# Revit family: 903-20-001 DN65-600
name_source: partatom
category: Pipe Accessories
units: mm (PartAtom-declared; Revit-internal decimal feet)

## family parameters
Always vertical = Yes
Cut with Voids When Loaded = No
Part Type = Valve - Breaks Into
Round Connector Dimension = Use Diameter
Shared = No
Work Plane-Based = No

## types (21) — shared parameters
1 = 1 mm  [stored 0.00328084 ft]
DN065_PN10/16 = 903-065-20-11000
DN080_PN10/16 = 903-080-20-11000
DN100_PN10/16 = 903-100-20-11000
DN125_PN10/16 = 903-125-20-11000
DN150_PN10/16 = 903-150-20-11000
DN200_PN10 = 903-200-20-01000
DN200_PN16 = 903-200-20-11000
DN250_PN10 = 903-250-20-01000
DN250_PN16 = 903-250-20-11000
DN300_PN10 = 903-300-20-01000
DN300_PN16 = 903-300-20-11000
DN350_PN10 = 903-350-20-01000
DN350_PN16 = 903-350-20-11000
DN400_PN10 = 903-400-20-01000
DN400_PN16 = 903-400-20-11000
DN450_PN10 = 903-450-20-01000
DN450_PN16 = 903-450-20-11000
DN500_PN10 = 903-500-20-01000
DN500_PN16 = 903-500-20-11000
DN600_PN10 = 903-600-20-01000
DN600_PN16 = 903-600-20-11000
Description_ = AVK SILENT CHECK VALVE, PN10/16
Search_table = 903-20-001 DN65-600
URL product pages = https://www.avkvalves.com
zero-valued in all types: Default Elevation

## per-type parameters (varying)
| type | Bodywall_thickness | C | C1 | D2 | DN | FL_T | Flange_thickness | Flange_thickness_2 | Flange_thickness_3 | ID | ID-1 | L | L/2 | L3 | L_ref | L_ref_2 | W | W1 | W2 | dim1 | dim2 | dim3 | w4 | wall_T |
| DN065_PN10/16 | 43 mm | 28 mm  [stored 0.0918635 ft] | 25 mm  [stored 0.082021 ft] | 69 mm | 65 mm | 4 mm  [stored 0.0131234 ft] | 19 mm  [stored 0.062336 ft] | 10 mm  [stored 0.0328084 ft] | 29 mm | 33 mm  [stored 0.108268 ft] | 32 mm | 140 mm | 70 mm | 42 mm  [stored 0.137795 ft] | 20 mm  [stored 0.0656168 ft] | 15 mm  [stored 0.0492126 ft] | 93 mm | 46 mm | 52 mm | 27 mm  [stored 0.0885827 ft] | 16 mm  [stored 0.0524934 ft] | 13 mm  [stored 0.0426509 ft] | 83 mm | 10 mm  [stored 0.0328084 ft] |
| DN080_PN10/16 | 50 mm | 36 mm | 32 mm | 75 mm | 80 mm | 4 mm  [stored 0.0131234 ft] | 19 mm  [stored 0.062336 ft] | 10 mm  [stored 0.0328084 ft] | 29 mm | 40 mm  [stored 0.131234 ft] | 39 mm  [stored 0.127953 ft] | 152 mm | 76 mm | 46 mm | 15 mm  [stored 0.0492126 ft] | 20 mm  [stored 0.0656168 ft] | 100 mm | 49 mm | 57 mm | 27 mm  [stored 0.0885827 ft] | 16 mm  [stored 0.0524934 ft] | 13 mm  [stored 0.0426509 ft] | 90 mm | 10 mm  [stored 0.0328084 ft] |
| DN100_PN10/16 | 60 mm | 46 mm | 41 mm | 88 mm | 100 mm | 4 mm  [stored 0.0131234 ft] | 19 mm  [stored 0.062336 ft] | 10 mm  [stored 0.0328084 ft] | 29 mm | 50 mm | 49 mm | 184 mm | 92 mm | 55 mm | 20 mm  [stored 0.0656168 ft] | 20 mm  [stored 0.0656168 ft] | 118 mm | 60 mm | 69 mm | 30 mm  [stored 0.0984252 ft] | 18 mm | 15 mm  [stored 0.0492126 ft] | 106 mm | 10 mm  [stored 0.0328084 ft] |
| DN125_PN10/16 | 73 mm | 51 mm | 46 mm | 101 mm | 125 mm | 4 mm  [stored 0.0131234 ft] | 19 mm  [stored 0.062336 ft] | 10 mm  [stored 0.0328084 ft] | 29 mm | 63 mm | 62 mm | 216 mm | 108 mm | 65 mm | 20 mm  [stored 0.0656168 ft] | 25 mm  [stored 0.082021 ft] | 135 mm | 70 mm | 81 mm | 33 mm  [stored 0.108268 ft] | 20 mm  [stored 0.0656168 ft] | 16 mm  [stored 0.0524934 ft] | 122 mm | 10 mm  [stored 0.0328084 ft] |
| DN150_PN10/16 | 85 mm | 61 mm | 55 mm | 113 mm | 150 mm | 4 mm  [stored 0.0131234 ft] | 19 mm  [stored 0.062336 ft] | 10 mm  [stored 0.0328084 ft] | 29 mm | 75 mm | 74 mm | 248 mm | 124 mm | 74 mm | 25 mm  [stored 0.082021 ft] | 35 mm  [stored 0.114829 ft] | 150 mm | 81 mm | 93 mm | 34 mm | 20 mm  [stored 0.0656168 ft] | 16 mm  [stored 0.0524934 ft] | 135 mm | 10 mm  [stored 0.0328084 ft] |
| DN200_PN10 | 110 mm | 84 mm | 76 mm | 135 mm | 200 mm | 4 mm  [stored 0.0131234 ft] | 20 mm  [stored 0.0656168 ft] | 10 mm  [stored 0.0328084 ft] | 30 mm  [stored 0.0984252 ft] | 100 mm | 99 mm | 317 mm | 159 mm | 95 mm | 40 mm  [stored 0.131234 ft] | 30 mm  [stored 0.0984252 ft] | 180 mm | 103 mm | 118 mm | 36 mm | 22 mm  [stored 0.0721785 ft] | 17 mm | 162 mm | 10 mm  [stored 0.0328084 ft] |
| DN200_PN16 | 110 mm | 84 mm | 76 mm | 135 mm | 200 mm | 4 mm  [stored 0.0131234 ft] | 20 mm  [stored 0.0656168 ft] | 10 mm  [stored 0.0328084 ft] | 30 mm  [stored 0.0984252 ft] | 100 mm | 99 mm | 317 mm | 159 mm | 95 mm | 40 mm  [stored 0.131234 ft] | 30 mm  [stored 0.0984252 ft] | 180 mm | 103 mm | 118 mm | 36 mm | 22 mm  [stored 0.0721785 ft] | 17 mm | 162 mm | 10 mm  [stored 0.0328084 ft] |
| DN250_PN10 | 135 mm | 118 mm | 106 mm | 165 mm | 250 mm | 4 mm  [stored 0.0131234 ft] | 22 mm  [stored 0.0721785 ft] | 11 mm  [stored 0.0360892 ft] | 33 mm  [stored 0.108268 ft] | 125 mm | 124 mm | 394 mm | 197 mm | 118 mm | 55 mm | 60 mm | 220 mm | 128 mm | 147 mm | 43 mm | 26 mm | 21 mm  [stored 0.0688976 ft] | 198 mm | 11 mm  [stored 0.0360892 ft] |
| DN250_PN16 | 135 mm | 118 mm | 106 mm | 165 mm | 250 mm | 4 mm  [stored 0.0131234 ft] | 22 mm  [stored 0.0721785 ft] | 11 mm  [stored 0.0360892 ft] | 33 mm  [stored 0.108268 ft] | 125 mm | 124 mm | 394 mm | 197 mm | 118 mm | 55 mm | 60 mm | 220 mm | 128 mm | 147 mm | 43 mm | 26 mm | 21 mm  [stored 0.0688976 ft] | 198 mm | 11 mm  [stored 0.0360892 ft] |
| DN300_PN10 | 160 mm | 16 mm  [stored 0.0524934 ft] | 14 mm  [stored 0.0459318 ft] | 188 mm | 300 mm | 5 mm  [stored 0.0164042 ft] | 23 mm | 11 mm  [stored 0.0360892 ft] | 34 mm | 150 mm | 149 mm | 362 mm | 181 mm | 109 mm | 60 mm | 40 mm  [stored 0.131234 ft] | 250 mm | 118 mm | 135 mm | 45 mm | 27 mm  [stored 0.0885827 ft] | 22 mm  [stored 0.0721785 ft] | 225 mm | 11 mm  [stored 0.0360892 ft] |
| DN300_PN16 | 160 mm | 16 mm  [stored 0.0524934 ft] | 14 mm  [stored 0.0459318 ft] | 188 mm | 300 mm | 5 mm  [stored 0.0164042 ft] | 23 mm | 11 mm  [stored 0.0360892 ft] | 34 mm | 150 mm | 149 mm | 362 mm | 181 mm | 109 mm | 60 mm | 40 mm  [stored 0.131234 ft] | 250 mm | 118 mm | 135 mm | 45 mm | 27 mm  [stored 0.0885827 ft] | 22 mm  [stored 0.0721785 ft] | 225 mm | 11 mm  [stored 0.0360892 ft] |
| DN350_PN10 | 185 mm | 36 mm | 32 mm | 218 mm | 350 mm | 5 mm  [stored 0.0164042 ft] | 25 mm  [stored 0.082021 ft] | 12 mm  [stored 0.0393701 ft] | 37 mm | 175 mm | 174 mm | 400 mm | 200 mm | 120 mm | 80 mm | 50 mm | 290 mm | 130 mm | 150 mm | 52 mm | 31 mm | 25 mm  [stored 0.082021 ft] | 261 mm | 12 mm  [stored 0.0393701 ft] |
| DN350_PN16 | 185 mm | 36 mm | 32 mm | 218 mm | 350 mm | 5 mm  [stored 0.0164042 ft] | 25 mm  [stored 0.082021 ft] | 12 mm  [stored 0.0393701 ft] | 37 mm | 175 mm | 174 mm | 400 mm | 200 mm | 120 mm | 80 mm | 50 mm | 290 mm | 130 mm | 150 mm | 52 mm | 31 mm | 25 mm  [stored 0.082021 ft] | 261 mm | 12 mm  [stored 0.0393701 ft] |
| DN400_PN10 | 210 mm | 50 mm | 45 mm | 238 mm | 400 mm | 5 mm  [stored 0.0164042 ft] | 27 mm  [stored 0.0885827 ft] | 13 mm  [stored 0.0426509 ft] | 40 mm  [stored 0.131234 ft] | 200 mm | 199 mm | 448 mm | 224 mm | 134 mm | 80 mm | 50 mm | 318 mm | 146 mm | 167 mm | 53 mm | 32 mm | 25 mm  [stored 0.082021 ft] | 286 mm | 13 mm  [stored 0.0426509 ft] |
| DN400_PN16 | 210 mm | 50 mm | 45 mm | 238 mm | 400 mm | 5 mm  [stored 0.0164042 ft] | 27 mm  [stored 0.0885827 ft] | 13 mm  [stored 0.0426509 ft] | 40 mm  [stored 0.131234 ft] | 200 mm | 199 mm | 448 mm | 224 mm | 134 mm | 80 mm | 50 mm | 318 mm | 146 mm | 167 mm | 53 mm | 32 mm | 25 mm  [stored 0.082021 ft] | 286 mm | 13 mm  [stored 0.0426509 ft] |
| DN450_PN10 | 235 mm | 10 mm  [stored 0.0328084 ft] | 9 mm  [stored 0.0295276 ft] | 272 mm | 450 mm | 6 mm  [stored 0.019685 ft] | 28 mm  [stored 0.0918635 ft] | 14 mm  [stored 0.0459318 ft] | 42 mm  [stored 0.137795 ft] | 225 mm | 224 mm | 477 mm | 239 mm | 143 mm | 90 mm | 90 mm | 320 mm | 155 mm | 178 mm | 43 mm | 26 mm | 21 mm  [stored 0.0688976 ft] | 288 mm | 14 mm  [stored 0.0459318 ft] |
| DN450_PN16 | 235 mm | 10 mm  [stored 0.0328084 ft] | 9 mm  [stored 0.0295276 ft] | 272 mm | 450 mm | 6 mm  [stored 0.019685 ft] | 28 mm  [stored 0.0918635 ft] | 14 mm  [stored 0.0459318 ft] | 42 mm  [stored 0.137795 ft] | 225 mm | 224 mm | 477 mm | 239 mm | 143 mm | 90 mm | 90 mm | 320 mm | 155 mm | 178 mm | 43 mm | 26 mm | 21 mm  [stored 0.0688976 ft] | 288 mm | 14 mm  [stored 0.0459318 ft] |
| DN500_PN10 | 260 mm | 9 mm  [stored 0.0295276 ft] | 8 mm  [stored 0.0262467 ft] | 304 mm | 500 mm | 6 mm  [stored 0.019685 ft] | 30 mm  [stored 0.0984252 ft] | 15 mm  [stored 0.0492126 ft] | 45 mm | 250 mm | 249 mm | 525 mm | 263 mm | 158 mm | 95 mm | 95 mm | 358 mm | 171 mm | 196 mm | 48 mm | 29 mm | 23 mm | 322 mm | 15 mm  [stored 0.0492126 ft] |
| DN500_PN16 | 260 mm | 9 mm  [stored 0.0295276 ft] | 8 mm  [stored 0.0262467 ft] | 304 mm | 500 mm | 6 mm  [stored 0.019685 ft] | 30 mm  [stored 0.0984252 ft] | 15 mm  [stored 0.0492126 ft] | 45 mm | 250 mm | 249 mm | 525 mm | 263 mm | 158 mm | 95 mm | 95 mm | 358 mm | 171 mm | 196 mm | 48 mm | 29 mm | 23 mm | 322 mm | 15 mm  [stored 0.0492126 ft] |
| DN600_PN10 | 310 mm | 27 mm  [stored 0.0885827 ft] | 24 mm | 357 mm | 600 mm | 6 mm  [stored 0.019685 ft] | 32 mm | 16 mm  [stored 0.0524934 ft] | 47 mm | 300 mm | 299 mm | 611 mm | 306 mm | 183 mm | 100 mm | 100 mm | 420 mm | 199 mm | 228 mm | 54 mm | 32 mm | 26 mm | 378 mm | 16 mm  [stored 0.0524934 ft] |
| DN600_PN16 | 310 mm | 27 mm  [stored 0.0885827 ft] | 24 mm | 357 mm | 600 mm | 6 mm  [stored 0.019685 ft] | 32 mm | 16 mm  [stored 0.0524934 ft] | 47 mm | 300 mm | 299 mm | 611 mm | 306 mm | 183 mm | 100 mm | 100 mm | 420 mm | 199 mm | 228 mm | 54 mm | 32 mm | 26 mm | 378 mm | 16 mm  [stored 0.0524934 ft] |

note: [stored X ft] marks values corroborated as IEEE doubles in the binary element streams (Revit-internal decimal feet)

## geometry (parser evidence)
native form markers: Sweep x5
no freeform markers — native parametric forms only
